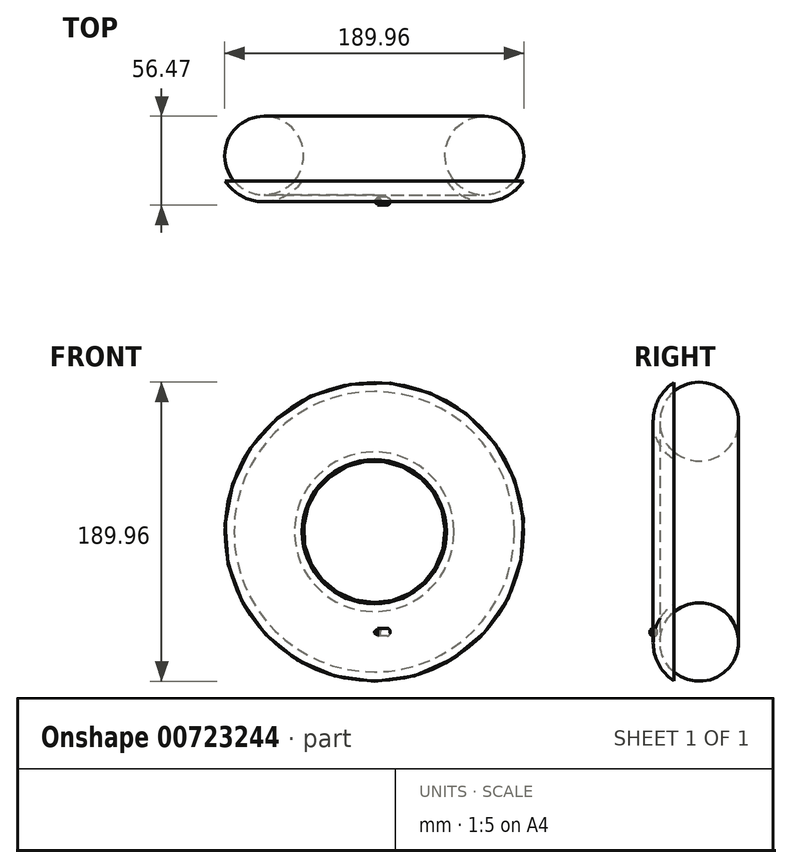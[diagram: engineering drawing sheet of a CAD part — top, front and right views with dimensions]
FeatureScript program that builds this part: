
annotation { "Feature Type Name" : "Feature", "Feature Type Description" : "" }
export const myFeature = defineFeature(function(context is Context, id is Id, definition is map)
    precondition{}
    {
        {
            var Q0;
            Q0=qCreatedBy(makeId("Top.planeOp"),FACE);
            var sketch = newSketch(context, id + "F0", { "sketchPlane" : qUnion([Q0])});
            skLineSegment(sketch, "E0", {"start": v(0, -99.68) * mm, "end": v(0, 102.32) * mm});
            skCircle(sketch, "E1", {"center": v(69.98, 0) * mm, "radius": 25 * mm});
            skArc(sketch, "E2", {"start": v(45.8, -15.84) * mm, "mid": v(70.17, -29.33) * mm, "end": v(94.72, -16.18) * mm});
            skLineSegment(sketch, "E3", {"start": v(94.72, -16.18) * mm, "end": v(45.8, -15.84) * mm});
            skSolve(sketch);
        }
        {
            var Q0;
            {var subQ0=sQuery(id+"F0.wireOp",EDGE,"E3");var subQ1=sQuery(id+"F0.wireOp",EDGE,"E1");var subQ2=makeQuery(id+"F0.imprint","INTERSECT",VERTEX,{"disambiguationData":[OD(0.0)],"derivedFrom":[subQ1,subQ0]});Q0=makeQuery(id+"F0.imprint","IMPRINT",FACE,{"disambiguationData":[TD([[makeQuery(id+"F0.imprint","IMPRINT",EDGE,{"disambiguationData":[TD([[subQ2,-1.0]])],"derivedFrom":subQ1}),1.0]])]});}
            var Q1;
            Q1=sQuery(id+"F0.wireOp",EDGE,"E0");
            revolve(context, id + "F1", {"surfaceOperationType" : NewSurfaceOperationType.NEW, "entities" : qUnion([Q0]), "axis" : qUnion([Q1]), "revolveType" : RevolveType.FULL});
        }
        {
            var Q0;
            {var subQ0=sQuery(id+"F0.wireOp",EDGE,"E3");var subQ1=sQuery(id+"F0.wireOp",EDGE,"E1");var subQ2=makeQuery(id+"F0.imprint","INTERSECT",VERTEX,{"disambiguationData":[OD(0.0)],"derivedFrom":[subQ1,subQ0]});Q0=makeQuery(id+"F0.imprint","IMPRINT",FACE,{"disambiguationData":[TD([[makeQuery(id+"F0.imprint","IMPRINT",EDGE,{"disambiguationData":[TD([[subQ2,1.0]])],"derivedFrom":subQ1}),1.0]])]});}
            var Q1;
            {var subQ4=sQuery(id+"F0.wireOp",EDGE,"E2");Q1=makeQuery(id+"F0.imprint","IMPRINT",FACE,{"disambiguationData":[TD([[makeQuery(id+"F0.imprint","IMPRINT",EDGE,{"derivedFrom":subQ4}),1.0]])]});}
            var Q2;
            Q2=sQuery(id+"F0.wireOp",EDGE,"E0");
            revolve(context, id + "F2", {"surfaceOperationType" : NewSurfaceOperationType.NEW, "entities" : qUnion([Q0, Q1]), "axis" : qUnion([Q2]), "revolveType" : RevolveType.FULL});
        }
        {
            var Q0;
            Q0=qCreatedBy(makeId("Right.planeOp"),FACE);
            var sketch = newSketch(context, id + "F3", { "sketchPlane" : qUnion([Q0])});
            skCircle(sketch, "E4", {"center": v(-28.97, -63.8) * mm, "radius": 2.5 * mm});
            skSolve(sketch);
        }
        {
            var Q0;
            Q0=makeQuery(id+"F3.imprint","IMPRINT",FACE,{"disambiguationData":[TD([[makeQuery(id+"F3.imprint","IMPRINT",EDGE,{"derivedFrom":sQuery(id+"F3.wireOp",EDGE,"E4")}),1.0]])]});
            extrude(context, id + "F4", {"entities" : qUnion([Q0]), "depth" : 10 * mm, "offsetDistance" : 25 * mm});
        }
        {
            var Q0;
            Q0=makeQuery(id+"F4.opExtrude","CAP_EDGE",EDGE,{"disambiguationData":[OSD([sQuery(id+"F3.wireOp",EDGE,"E4")])],"isStart":true});
            var Q1;
            Q1=makeQuery(id+"F4.opExtrude","CAP_EDGE",EDGE,{"disambiguationData":[OSD([sQuery(id+"F3.wireOp",EDGE,"E4")])],"isStart":false});
            fillet(context, id + "F5", {"entities" : qUnion([Q0, Q1]), "radius" : 2 * mm, "tangentPropagation" : true, "allowEdgeOverflow" : false});
        }
    });
